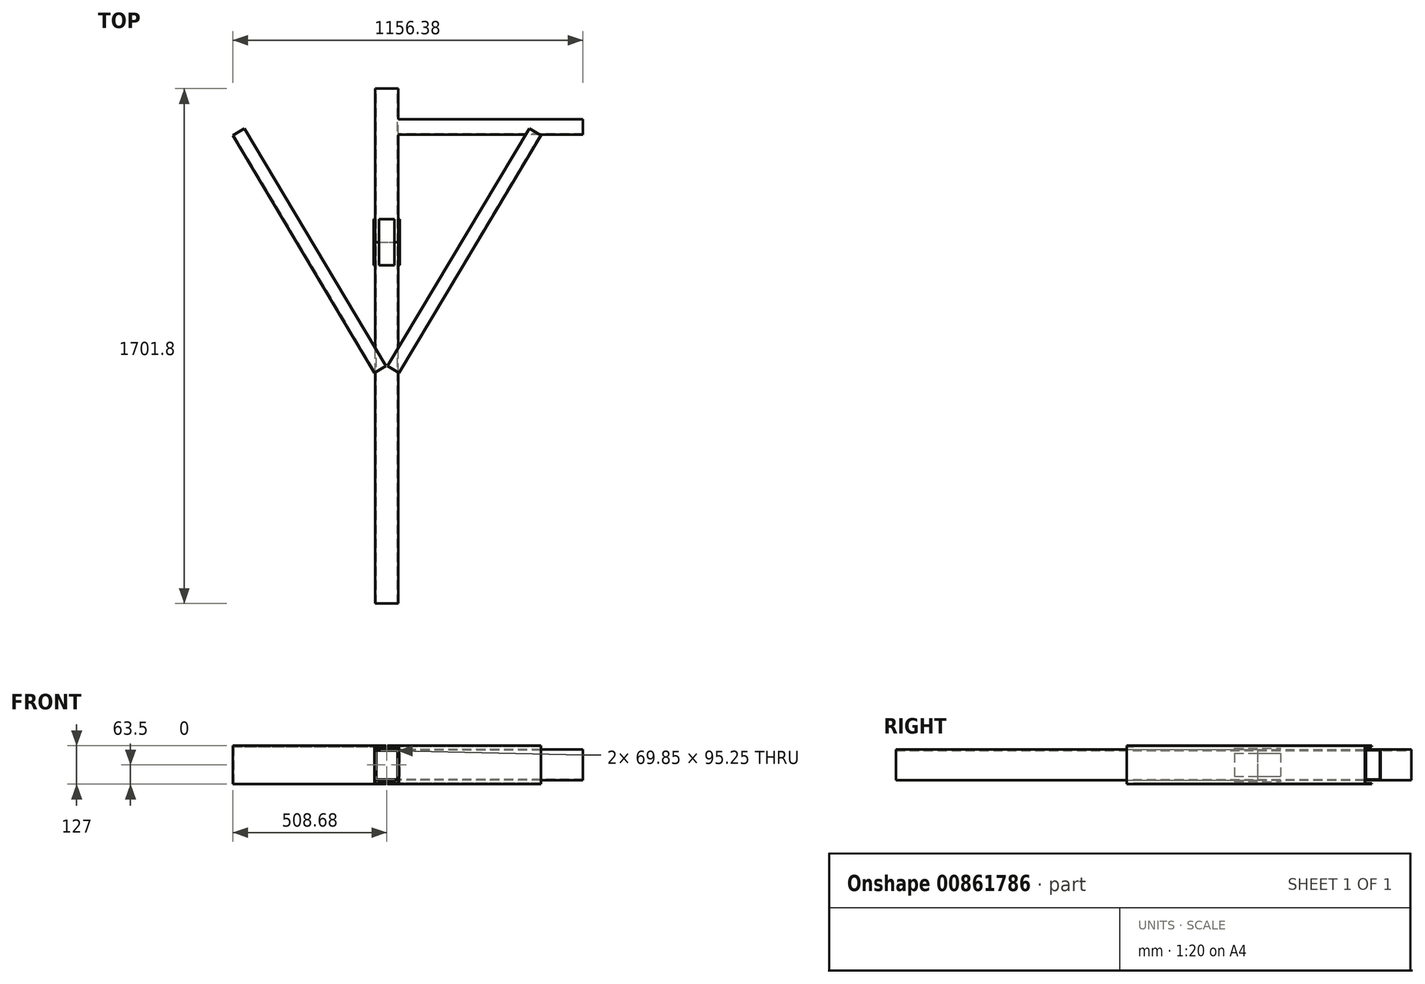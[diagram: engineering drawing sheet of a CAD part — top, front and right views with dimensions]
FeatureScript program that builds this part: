
annotation { "Feature Type Name" : "Feature", "Feature Type Description" : "" }
export const myFeature = defineFeature(function(context is Context, id is Id, definition is map)
    precondition{}
    {
        {
            var Q0;
            Q0=qCreatedBy(makeId("Front.planeOp"),FACE);
            var sketch = newSketch(context, id + "F0", { "sketchPlane" : qUnion([Q0])});
            skLineSegment(sketch, "E0.bottom", {"start": v(-38.1, 50.8) * mm, "end": v(38.1, 50.8) * mm});
            skLineSegment(sketch, "E0.top", {"start": v(-38.1, -50.8) * mm, "end": v(38.1, -50.8) * mm});
            skLineSegment(sketch, "E0.left", {"start": v(-38.1, 50.8) * mm, "end": v(-38.1, -50.8) * mm});
            skLineSegment(sketch, "E0.right", {"start": v(38.1, 50.8) * mm, "end": v(38.1, -50.8) * mm});
            skLineSegment(sketch, "E1", {"start": v(38.1, 50.8) * mm, "end": v(-38.1, -50.8) * mm, "construction": true});
            skSolve(sketch);
        }
        {
            var Q0;
            Q0 = qSketchRegion(id + "F0", true);
            extrude(context, id + "F1", {"entities" : qUnion([Q0]), "depth" : 355.6 * mm, "offsetDistance" : 25.4 * mm, "hasSecondDirection" : true, "secondDirectionOppositeDirection" : true, "secondDirectionDepth" : 152.4 * mm});
        }
        {
            var Q0;
            Q0=makeQuery(id+"F1.opExtrude","CAP_FACE",FACE,{"disambiguationData":[OSD([sQuery(id+"F0.wireOp",EDGE,"E0.bottom"),sQuery(id+"F0.wireOp",EDGE,"E0.top"),sQuery(id+"F0.wireOp",EDGE,"E0.left"),sQuery(id+"F0.wireOp",EDGE,"E0.right")])],"isStart":false});
            var Q1;
            Q1=makeQuery(id+"F1.opExtrude","CAP_FACE",FACE,{"disambiguationData":[OSD([sQuery(id+"F0.wireOp",EDGE,"E0.bottom"),sQuery(id+"F0.wireOp",EDGE,"E0.top"),sQuery(id+"F0.wireOp",EDGE,"E0.left"),sQuery(id+"F0.wireOp",EDGE,"E0.right")])],"isStart":true});
            shell(context, id + "F2", {"entities" : qUnion([Q0, Q1]), "thickness" : 3.17 * mm});
        }
        {
            var Q0;
            Q0=makeQuery(id+"F1.opExtrude","SWEPT_FACE",FACE,{"disambiguationData":[OSD([sQuery(id+"F0.wireOp",EDGE,"E0.right")])]});
            var sketch = newSketch(context, id + "F3", { "sketchPlane" : qUnion([Q0])});
            skLineSegment(sketch, "E2.bottom", {"start": v(0, 50.8) * mm, "end": v(50.8, 50.8) * mm});
            skLineSegment(sketch, "E2.top", {"start": v(0, -50.8) * mm, "end": v(50.8, -50.8) * mm});
            skLineSegment(sketch, "E2.left", {"start": v(0, 50.8) * mm, "end": v(0, -50.8) * mm});
            skLineSegment(sketch, "E2.right", {"start": v(50.8, 50.8) * mm, "end": v(50.8, -50.8) * mm});
            skSolve(sketch);
        }
        {
            var Q0;
            Q0 = qSketchRegion(id + "F3", true);
            extrude(context, id + "F4", {"entities" : qUnion([Q0]), "operationType" : NewBodyOperationType.ADD, "depth" : 609.6 * mm, "offsetDistance" : 25.4 * mm});
        }
        {
            var Q0;
            Q0=makeQuery(id+"F4.opExtrude","CAP_FACE",FACE,{"disambiguationData":[OSD([sQuery(id+"F3.wireOp",EDGE,"E2.bottom"),sQuery(id+"F3.wireOp",EDGE,"E2.top"),sQuery(id+"F3.wireOp",EDGE,"E2.left"),sQuery(id+"F3.wireOp",EDGE,"E2.right")])],"isStart":false});
            shell(context, id + "F5", {"entities" : qUnion([Q0]), "thickness" : 2.54 * mm});
        }
        {
            var Q0;
            Q0=makeQuery(id+"F1.opExtrude","CAP_FACE",FACE,{"disambiguationData":[OSD([sQuery(id+"F0.wireOp",EDGE,"E0.bottom"),sQuery(id+"F0.wireOp",EDGE,"E0.top"),sQuery(id+"F0.wireOp",EDGE,"E0.left"),sQuery(id+"F0.wireOp",EDGE,"E0.right")])],"isStart":false});
            var sketch = newSketch(context, id + "F6", { "sketchPlane" : qUnion([Q0])});
            skLineSegment(sketch, "E3.bottom", {"start": v(-38.1, -38.1) * mm, "end": v(-42.86, -38.1) * mm});
            skLineSegment(sketch, "E3.top", {"start": v(-38.1, 38.1) * mm, "end": v(-42.86, 38.1) * mm});
            skLineSegment(sketch, "E3.left", {"start": v(-38.1, 38.1) * mm, "end": v(-38.1, -38.1) * mm});
            skLineSegment(sketch, "E3.right", {"start": v(-42.86, 38.1) * mm, "end": v(-42.86, -38.1) * mm});
            skLineSegment(sketch, "E4.bottom", {"start": v(-25.4, 50.8) * mm, "end": v(25.4, 50.8) * mm});
            skLineSegment(sketch, "E4.top", {"start": v(-25.4, 55.56) * mm, "end": v(25.4, 55.56) * mm});
            skLineSegment(sketch, "E4.left", {"start": v(25.4, 50.8) * mm, "end": v(25.4, 55.56) * mm});
            skLineSegment(sketch, "E4.right", {"start": v(-25.4, 50.8) * mm, "end": v(-25.4, 55.56) * mm});
            skLineSegment(sketch, "E5.bottom", {"start": v(38.1, -38.1) * mm, "end": v(42.86, -38.1) * mm});
            skLineSegment(sketch, "E5.top", {"start": v(38.1, 38.1) * mm, "end": v(42.86, 38.1) * mm});
            skLineSegment(sketch, "E5.left", {"start": v(38.1, 38.1) * mm, "end": v(38.1, -38.1) * mm});
            skLineSegment(sketch, "E5.right", {"start": v(42.86, 38.1) * mm, "end": v(42.86, -38.1) * mm});
            skLineSegment(sketch, "E6.bottom", {"start": v(-25.4, -50.8) * mm, "end": v(25.4, -50.8) * mm});
            skLineSegment(sketch, "E6.top", {"start": v(-25.4, -55.56) * mm, "end": v(25.4, -55.56) * mm});
            skLineSegment(sketch, "E6.left", {"start": v(25.4, -50.8) * mm, "end": v(25.4, -55.56) * mm});
            skLineSegment(sketch, "E6.right", {"start": v(-25.4, -50.8) * mm, "end": v(-25.4, -55.56) * mm});
            skLineSegment(sketch, "E7", {"start": v(0, 50.8) * mm, "end": v(0, -50.8) * mm, "construction": true});
            skLineSegment(sketch, "E8", {"start": v(38.1, 0) * mm, "end": v(-38.1, 0) * mm, "construction": true});
            skSolve(sketch);
        }
        {
            var Q0;
            Q0 = qSketchRegion(id + "F6", true);
            extrude(context, id + "F7", {"entities" : qUnion([Q0]), "operationType" : NewBodyOperationType.ADD, "endBound" : BoundingType.SYMMETRIC, "depth" : 152.4 * mm, "offsetDistance" : 25.4 * mm});
        }
        {
            var Q0;
            Q0=makeQuery(id+"F1.opExtrude","CAP_FACE",FACE,{"disambiguationData":[OSD([sQuery(id+"F0.wireOp",EDGE,"E0.bottom"),sQuery(id+"F0.wireOp",EDGE,"E0.top"),sQuery(id+"F0.wireOp",EDGE,"E0.left"),sQuery(id+"F0.wireOp",EDGE,"E0.right")])],"isStart":false});
            var sketch = newSketch(context, id + "F8", { "sketchPlane" : qUnion([Q0])});
            skLineSegment(sketch, "E9.bottom", {"start": v(-38.1, -50.8) * mm, "end": v(38.1, -50.8) * mm});
            skLineSegment(sketch, "E9.top", {"start": v(-38.1, 50.8) * mm, "end": v(38.1, 50.8) * mm});
            skLineSegment(sketch, "E9.left", {"start": v(-38.1, -50.8) * mm, "end": v(-38.1, 50.8) * mm});
            skLineSegment(sketch, "E9.right", {"start": v(38.1, -50.8) * mm, "end": v(38.1, 50.8) * mm});
            skLineSegment(sketch, "E10.bottom", {"start": v(34.92, 47.63) * mm, "end": v(-34.93, 47.63) * mm});
            skLineSegment(sketch, "E10.top", {"start": v(34.92, -47.62) * mm, "end": v(-34.93, -47.62) * mm});
            skLineSegment(sketch, "E10.left", {"start": v(34.92, 47.63) * mm, "end": v(34.92, -47.62) * mm});
            skLineSegment(sketch, "E10.right", {"start": v(-34.93, 47.63) * mm, "end": v(-34.93, -47.62) * mm});
            skSolve(sketch);
        }
        {
            var Q0;
            Q0 = qSketchRegion(id + "F8", true);
            extrude(context, id + "F9", {"entities" : qUnion([Q0]), "depth" : 1193.8 * mm, "offsetDistance" : 25.4 * mm});
        }
        {
            var Q0;
            Q0=qCreatedBy(makeId("Top.planeOp"),FACE);
            var sketch = newSketch(context, id + "F10", { "sketchPlane" : qUnion([Q0])});
            skLineSegment(sketch, "E11.bottom", {"start": v(-508.68, -1.69) * mm, "end": v(-470.49, 21.05) * mm});
            skLineSegment(sketch, "E11.top", {"start": v(-40.94, -787.4) * mm, "end": v(-2.74, -764.66) * mm});
            skLineSegment(sketch, "E11.left", {"start": v(-508.68, -1.69) * mm, "end": v(-40.94, -787.4) * mm});
            skLineSegment(sketch, "E11.right", {"start": v(-470.49, 21.05) * mm, "end": v(-2.74, -764.66) * mm});
            skLineSegment(sketch, "E12", {"start": v(-505.85, 0) * mm, "end": v(-38.1, -785.71) * mm, "construction": true});
            skSolve(sketch);
        }
        {
            var Q0;
            Q0 = qSketchRegion(id + "F10", true);
            extrude(context, id + "F11", {"entities" : qUnion([Q0]), "endBound" : BoundingType.SYMMETRIC, "depth" : 127 * mm, "offsetDistance" : 25.4 * mm});
        }
        {
            var Q0;
            Q0=makeQuery(id+"F11.opExtrude","SWEPT_FACE",FACE,{"disambiguationData":[OSD([sQuery(id+"F10.wireOp",EDGE,"E11.right")])]});
            var Q1;
            Q1=makeQuery(id+"F11.opExtrude","SWEPT_FACE",FACE,{"disambiguationData":[OSD([sQuery(id+"F10.wireOp",EDGE,"E11.top")])]});
            var Q2;
            Q2=makeQuery(id+"F11.opExtrude","SWEPT_FACE",FACE,{"disambiguationData":[OSD([sQuery(id+"F10.wireOp",EDGE,"E11.bottom")])]});
            shell(context, id + "F12", {"entities" : qUnion([Q0, Q1, Q2]), "thickness" : 3.17 * mm});
        }
        {
            var Q0;
            Q0=makeQuery(id+"F11.opExtrude","SWEPT_BODY",BODY,{"disambiguationData":[OSD([sQuery(id+"F10.wireOp",EDGE,"E11.bottom"),sQuery(id+"F10.wireOp",EDGE,"E11.top"),sQuery(id+"F10.wireOp",EDGE,"E11.left"),sQuery(id+"F10.wireOp",EDGE,"E11.right")])]});
            var Q1;
            Q1=qCreatedBy(makeId("Right.planeOp"),FACE);
            mirror(context, id + "F13", {"entities" : qUnion([Q0]), "mirrorPlane" : qUnion([Q1])});
        }
    });
